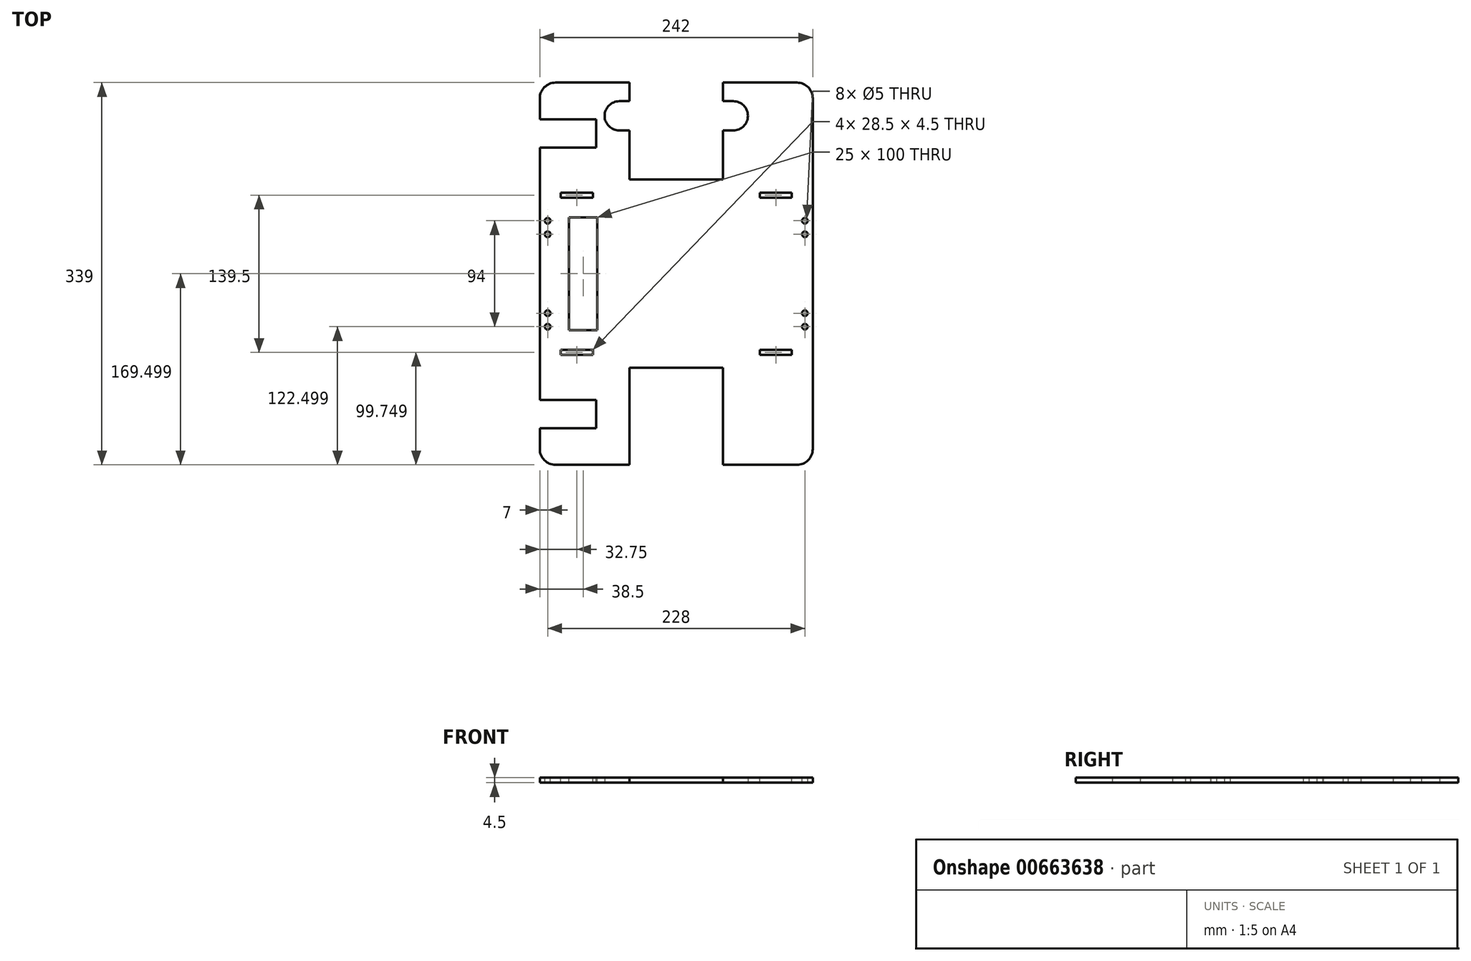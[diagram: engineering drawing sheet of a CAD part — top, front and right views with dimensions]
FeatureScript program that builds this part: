
annotation { "Feature Type Name" : "Feature", "Feature Type Description" : "" }
export const myFeature = defineFeature(function(context is Context, id is Id, definition is map)
    precondition{}
    {
        {
            var Q0;
            Q0=qCreatedBy(makeId("Top.planeOp"),FACE);
            var sketch = newSketch(context, id + "F0", { "sketchPlane" : qUnion([Q0])});
            skLineSegment(sketch, "E0.bottom", {"start": v(-109.12, 146.8) * mm, "end": v(104.88, 146.8) * mm});
            skLineSegment(sketch, "E0.top", {"start": v(-109.12, -192.2) * mm, "end": v(104.88, -192.2) * mm});
            skLineSegment(sketch, "E0.left", {"start": v(-123.12, 132.8) * mm, "end": v(-123.12, -178.2) * mm});
            skLineSegment(sketch, "E0.right", {"start": v(118.88, 132.8) * mm, "end": v(118.88, -178.2) * mm});
            skPoint(sketch, "E1.visualSharp", {"position": v(-123.12, 146.8) * mm});
            skArc(sketch, "E1.filletArc", {"start": v(-109.12, 146.8) * mm, "mid": v(-119.02, 142.7) * mm, "end": v(-123.12, 132.8) * mm});
            skPoint(sketch, "E2.visualSharp", {"position": v(118.88, 146.8) * mm});
            skArc(sketch, "E2.filletArc", {"start": v(118.88, 132.8) * mm, "mid": v(114.78, 142.7) * mm, "end": v(104.88, 146.8) * mm});
            skPoint(sketch, "E3.visualSharp", {"position": v(118.88, -192.2) * mm});
            skArc(sketch, "E3.filletArc", {"start": v(104.88, -192.2) * mm, "mid": v(114.78, -188.1) * mm, "end": v(118.88, -178.2) * mm});
            skPoint(sketch, "E4.visualSharp", {"position": v(-123.12, -192.2) * mm});
            skArc(sketch, "E4.filletArc", {"start": v(-123.12, -178.2) * mm, "mid": v(-119.02, -188.1) * mm, "end": v(-109.12, -192.2) * mm});
            skLineSegment(sketch, "E5.bottom", {"start": v(-52.62, 130.3) * mm, "end": v(48.38, 130.3) * mm});
            skLineSegment(sketch, "E5.top", {"start": v(-52.62, 104.3) * mm, "end": v(48.38, 104.3) * mm});
            skLineSegment(sketch, "E5.left", {"start": v(-65.62, 117.3) * mm, "end": v(-65.62, 117.3) * mm});
            skLineSegment(sketch, "E5.right", {"start": v(61.38, 117.3) * mm, "end": v(61.38, 117.3) * mm});
            skPoint(sketch, "E6", {"position": v(0, 146.8) * mm});
            skPoint(sketch, "E7", {"position": v(-2.12, 104.3) * mm});
            skPoint(sketch, "E8.visualSharp", {"position": v(-65.62, 130.3) * mm});
            skArc(sketch, "E8.filletArc", {"start": v(-52.62, 130.3) * mm, "mid": v(-61.81, 126.5) * mm, "end": v(-65.62, 117.3) * mm});
            skPoint(sketch, "E9.visualSharp", {"position": v(-65.62, 104.3) * mm});
            skArc(sketch, "E9.filletArc", {"start": v(-65.62, 117.3) * mm, "mid": v(-61.81, 108.12) * mm, "end": v(-52.62, 104.3) * mm});
            skPoint(sketch, "E10.visualSharp", {"position": v(61.38, 104.3) * mm});
            skArc(sketch, "E10.filletArc", {"start": v(48.38, 104.3) * mm, "mid": v(57.57, 108.12) * mm, "end": v(61.38, 117.3) * mm});
            skPoint(sketch, "E11.visualSharp", {"position": v(61.38, 130.3) * mm});
            skArc(sketch, "E11.filletArc", {"start": v(61.38, 117.3) * mm, "mid": v(57.57, 126.5) * mm, "end": v(48.38, 130.3) * mm});
            skSolve(sketch);
        }
        {
            var Q0;
            Q0=qSketchRegion(id+"F0",true);
            extrude(context, id + "F1", {"entities" : qUnion([Q0]), "depth" : 4.5 * mm, "offsetDistance" : 25 * mm});
        }
        {
            var Q0;
            Q0=makeQuery(id+"F1.opExtrude","CAP_FACE",FACE,{"disambiguationData":[OSD([sQuery(id+"F0.wireOp",EDGE,"E0.bottom"),sQuery(id+"F0.wireOp",EDGE,"E0.top"),sQuery(id+"F0.wireOp",EDGE,"E0.left"),sQuery(id+"F0.wireOp",EDGE,"E0.right"),sQuery(id+"F0.wireOp",EDGE,"E1.filletArc"),sQuery(id+"F0.wireOp",EDGE,"E2.filletArc"),sQuery(id+"F0.wireOp",EDGE,"E3.filletArc"),sQuery(id+"F0.wireOp",EDGE,"E4.filletArc"),sQuery(id+"F0.wireOp",EDGE,"E5.bottom"),sQuery(id+"F0.wireOp",EDGE,"E5.top"),sQuery(id+"F0.wireOp",EDGE,"E8.filletArc"),sQuery(id+"F0.wireOp",EDGE,"E9.filletArc"),sQuery(id+"F0.wireOp",EDGE,"E10.filletArc"),sQuery(id+"F0.wireOp",EDGE,"E11.filletArc")])],"isStart":false});
            var sketch = newSketch(context, id + "F2", { "sketchPlane" : qUnion([Q0])});
            skLineSegment(sketch, "E12", {"start": v(-2.12, -22.7) * mm, "end": v(-2.12, 146.8) * mm, "construction": true});
            skLineSegment(sketch, "E13", {"start": v(-123.12, -22.7) * mm, "end": v(80.84, -22.7) * mm, "construction": true});
            skCircle(sketch, "E14", {"center": v(-2.12, 101.8) * mm, "radius": 41.5 * mm, "construction": true});
            skLineSegment(sketch, "E15.bottom", {"start": v(-104.62, 44.8) * mm, "end": v(-76.12, 44.8) * mm});
            skLineSegment(sketch, "E15.top", {"start": v(-104.62, 49.3) * mm, "end": v(-76.12, 49.3) * mm});
            skLineSegment(sketch, "E15.left", {"start": v(-104.62, 44.8) * mm, "end": v(-104.62, 49.3) * mm});
            skLineSegment(sketch, "E15.right", {"start": v(-76.12, 44.8) * mm, "end": v(-76.12, 49.3) * mm});
            skCircle(sketch, "E16", {"center": v(-116.12, 24.3) * mm, "radius": 2.5 * mm});
            skCircle(sketch, "E17", {"center": v(-116.12, 12.3) * mm, "radius": 2.5 * mm});
            skPoint(sketch, "E18", {"position": v(-2.12, 146.8) * mm});
            skCircle(sketch, "E19.MirrorC", {"center": v(-116.12, -57.7) * mm, "radius": 2.5 * mm});
            skCircle(sketch, "E20.MirrorC", {"center": v(-116.12, -69.7) * mm, "radius": 2.5 * mm});
            skLineSegment(sketch, "E21.MirrorCS", {"start": v(-76.12, -90.2) * mm, "end": v(-76.12, -94.7) * mm});
            skLineSegment(sketch, "E22.MirrorCS", {"start": v(-104.62, -94.7) * mm, "end": v(-76.12, -94.7) * mm});
            skLineSegment(sketch, "E23.MirrorCS", {"start": v(-104.62, -90.2) * mm, "end": v(-76.12, -90.2) * mm});
            skLineSegment(sketch, "E24.MirrorCS", {"start": v(-104.62, -90.2) * mm, "end": v(-104.62, -94.7) * mm});
            skCircle(sketch, "E25.MirrorC", {"center": v(-2.12, -147.2) * mm, "radius": 41.5 * mm, "construction": true});
            skLineSegment(sketch, "E26.MirrorCS", {"start": v(71.88, 44.8) * mm, "end": v(71.88, 49.3) * mm});
            skLineSegment(sketch, "E27.MirrorCS", {"start": v(100.38, 44.8) * mm, "end": v(100.38, 49.3) * mm});
            skLineSegment(sketch, "E28.MirrorCS", {"start": v(71.88, -90.2) * mm, "end": v(71.88, -94.7) * mm});
            skLineSegment(sketch, "E29.MirrorCS", {"start": v(100.38, -90.2) * mm, "end": v(100.38, -94.7) * mm});
            skCircle(sketch, "E30.MirrorC", {"center": v(111.88, 24.3) * mm, "radius": 2.5 * mm});
            skCircle(sketch, "E31.MirrorC", {"center": v(111.88, 12.3) * mm, "radius": 2.5 * mm});
            skCircle(sketch, "E32.MirrorC", {"center": v(111.88, -57.7) * mm, "radius": 2.5 * mm});
            skCircle(sketch, "E33.MirrorC", {"center": v(111.88, -69.7) * mm, "radius": 2.5 * mm});
            skLineSegment(sketch, "E34.MirrorCS", {"start": v(100.38, 49.3) * mm, "end": v(71.88, 49.3) * mm});
            skLineSegment(sketch, "E35.MirrorCS", {"start": v(100.38, 44.8) * mm, "end": v(71.88, 44.8) * mm});
            skLineSegment(sketch, "E36.MirrorCS", {"start": v(100.38, -94.7) * mm, "end": v(71.88, -94.7) * mm});
            skLineSegment(sketch, "E37.MirrorCS", {"start": v(100.38, -90.2) * mm, "end": v(71.88, -90.2) * mm});
            skLineSegment(sketch, "E38.bottom", {"start": v(-72.12, -72.7) * mm, "end": v(-97.12, -72.7) * mm});
            skLineSegment(sketch, "E38.top", {"start": v(-72.12, 27.3) * mm, "end": v(-97.12, 27.3) * mm});
            skLineSegment(sketch, "E38.left", {"start": v(-72.12, -72.7) * mm, "end": v(-72.12, 27.3) * mm});
            skLineSegment(sketch, "E38.right", {"start": v(-97.12, -72.7) * mm, "end": v(-97.12, 27.3) * mm});
            skPoint(sketch, "E38.middle", {"position": v(-84.62, -22.7) * mm});
            skLineSegment(sketch, "E39.bottom", {"start": v(-73.12, 89.3) * mm, "end": v(-123.12, 89.3) * mm});
            skLineSegment(sketch, "E39.top", {"start": v(-73.12, 114.3) * mm, "end": v(-123.12, 114.3) * mm});
            skLineSegment(sketch, "E39.left", {"start": v(-73.12, 89.3) * mm, "end": v(-73.12, 114.3) * mm});
            skLineSegment(sketch, "E40.MirrorCS", {"start": v(-73.12, -134.7) * mm, "end": v(-73.12, -159.7) * mm});
            skLineSegment(sketch, "E41.MirrorCS", {"start": v(-73.12, -159.7) * mm, "end": v(-123.12, -159.7) * mm});
            skLineSegment(sketch, "E42.MirrorCS", {"start": v(-73.12, -134.7) * mm, "end": v(-123.12, -134.7) * mm});
            skLineSegment(sketch, "E43", {"start": v(-123.12, 114.3) * mm, "end": v(-123.12, 89.3) * mm});
            skLineSegment(sketch, "E44.MirrorCS", {"start": v(-123.12, -159.7) * mm, "end": v(-123.12, -134.7) * mm});
            skLineSegment(sketch, "E45.bottom", {"start": v(-43.62, 60.8) * mm, "end": v(39.38, 60.8) * mm});
            skLineSegment(sketch, "E45.top", {"start": v(-43.62, 146.8) * mm, "end": v(39.38, 146.8) * mm});
            skLineSegment(sketch, "E45.left", {"start": v(-43.62, 60.8) * mm, "end": v(-43.62, 146.8) * mm});
            skLineSegment(sketch, "E45.right", {"start": v(39.38, 60.8) * mm, "end": v(39.38, 146.8) * mm});
            skPoint(sketch, "E45.middle", {"position": v(-2.12, 103.8) * mm});
            skLineSegment(sketch, "E46.MirrorCS", {"start": v(39.38, -106.2) * mm, "end": v(39.38, -192.2) * mm});
            skLineSegment(sketch, "E47.MirrorCS", {"start": v(-43.62, -106.2) * mm, "end": v(39.38, -106.2) * mm});
            skLineSegment(sketch, "E48.MirrorCS", {"start": v(-43.62, -106.2) * mm, "end": v(-43.62, -192.2) * mm});
            skLineSegment(sketch, "E49.MirrorCS", {"start": v(-43.62, -192.2) * mm, "end": v(39.38, -192.2) * mm});
            skSolve(sketch);
        }
        {
            var Q0;
            Q0 = qSketchRegion(id + "F2", true);
            extrude(context, id + "F3", {"entities" : qUnion([Q0]), "operationType" : NewBodyOperationType.REMOVE, "oppositeDirection" : true, "depth" : 25 * mm, "offsetDistance" : 25 * mm});
        }
    });
